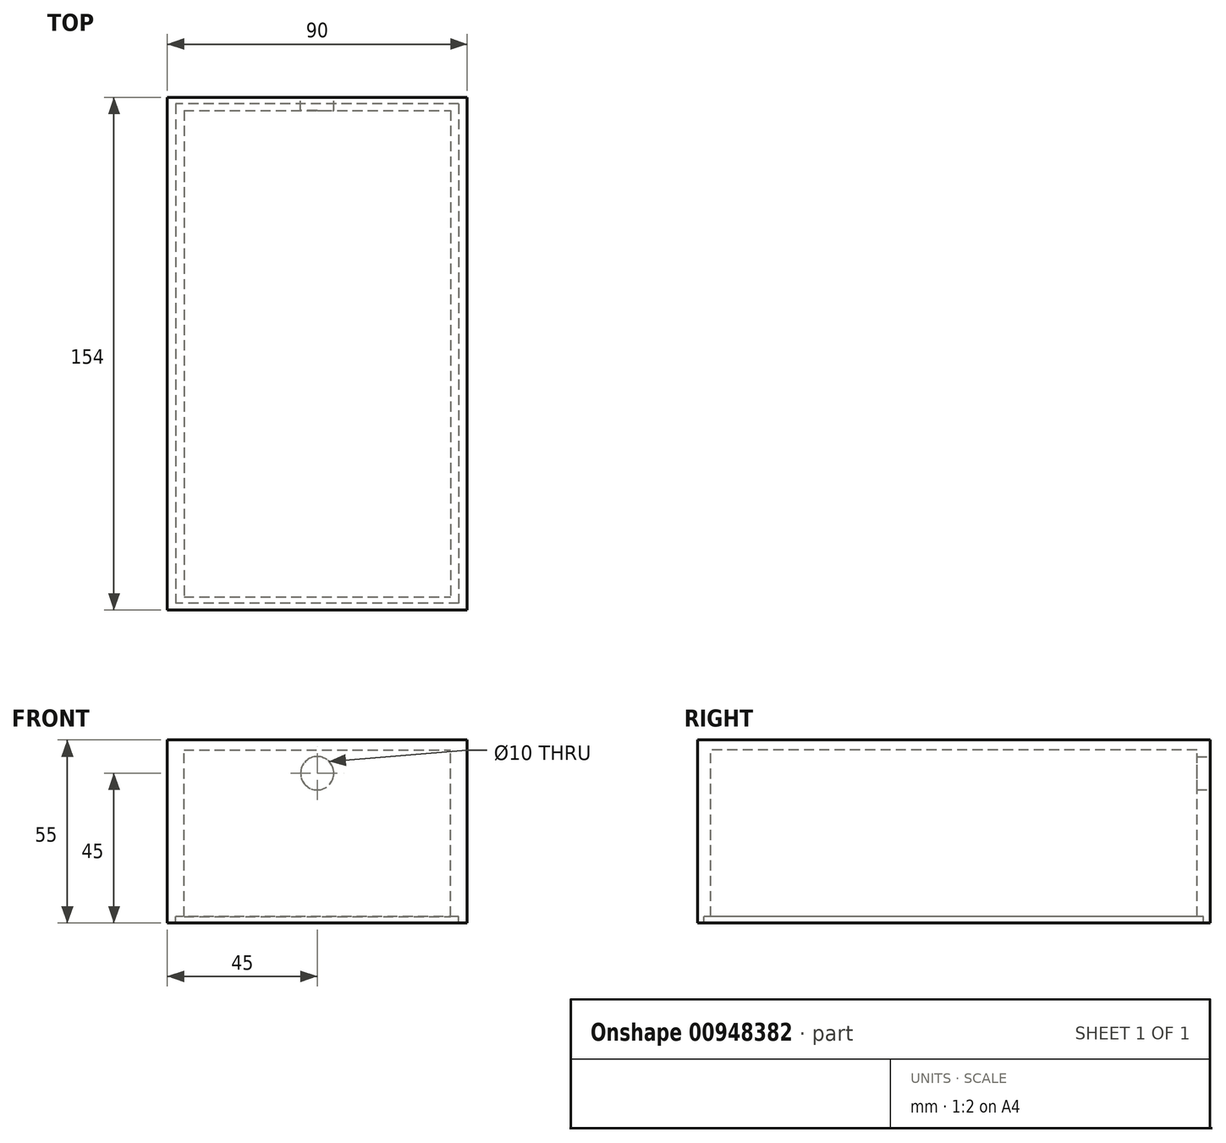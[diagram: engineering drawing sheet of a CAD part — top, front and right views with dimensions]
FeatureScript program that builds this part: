
annotation { "Feature Type Name" : "Feature", "Feature Type Description" : "" }
export const myFeature = defineFeature(function(context is Context, id is Id, definition is map)
    precondition{}
    {
        {
            var Q0;
            Q0=qCreatedBy(makeId("Top.planeOp"),FACE);
            var sketch = newSketch(context, id + "F0", { "sketchPlane" : qUnion([Q0])});
            skLineSegment(sketch, "E0.bottom", {"start": v(-45, 77) * mm, "end": v(45, 77) * mm});
            skLineSegment(sketch, "E0.top", {"start": v(-45, -77) * mm, "end": v(45, -77) * mm});
            skLineSegment(sketch, "E0.left", {"start": v(-45, 77) * mm, "end": v(-45, -77) * mm});
            skLineSegment(sketch, "E0.right", {"start": v(45, 77) * mm, "end": v(45, -77) * mm});
            skPoint(sketch, "E0.middle", {"position": v(0, 0) * mm});
            skLineSegment(sketch, "E1.bottom", {"start": v(-40, 73) * mm, "end": v(40, 73) * mm});
            skLineSegment(sketch, "E1.top", {"start": v(-40, -73) * mm, "end": v(40, -73) * mm});
            skLineSegment(sketch, "E1.left", {"start": v(-40, 73) * mm, "end": v(-40, -73) * mm});
            skLineSegment(sketch, "E1.right", {"start": v(40, 73) * mm, "end": v(40, -73) * mm});
            skLineSegment(sketch, "E2.bottom", {"start": v(42.5, 75) * mm, "end": v(-42.5, 75) * mm});
            skLineSegment(sketch, "E2.top", {"start": v(42.5, -75) * mm, "end": v(-42.5, -75) * mm});
            skLineSegment(sketch, "E2.left", {"start": v(42.5, 75) * mm, "end": v(42.5, -75) * mm});
            skLineSegment(sketch, "E2.right", {"start": v(-42.5, 75) * mm, "end": v(-42.5, -75) * mm});
            skSolve(sketch);
        }
        {
            var Q0;
            Q0=makeQuery(id+"F0.imprint","IMPRINT",FACE,{"disambiguationData":[TD([[makeQuery(id+"F0.imprint","IMPRINT",EDGE,{"derivedFrom":sQuery(id+"F0.wireOp",EDGE,"E1.bottom")}),-1.0]])]});
            var Q1;
            Q1=makeQuery(id+"F0.imprint","IMPRINT",FACE,{"disambiguationData":[TD([[makeQuery(id+"F0.imprint","IMPRINT",EDGE,{"derivedFrom":sQuery(id+"F0.wireOp",EDGE,"E1.bottom")}),1.0]])]});
            var Q2;
            Q2=makeQuery(id+"F0.imprint","IMPRINT",FACE,{"disambiguationData":[TD([[makeQuery(id+"F0.imprint","IMPRINT",EDGE,{"derivedFrom":sQuery(id+"F0.wireOp",EDGE,"E0.bottom")}),-1.0]])]});
            extrude(context, id + "F1", {"entities" : qUnion([Q0, Q1, Q2]), "depth" : 3 * mm, "offsetDistance" : 25 * mm});
        }
        {
            var Q0;
            Q0=makeQuery(id+"F0.imprint","IMPRINT",FACE,{"disambiguationData":[TD([[makeQuery(id+"F0.imprint","IMPRINT",EDGE,{"derivedFrom":sQuery(id+"F0.wireOp",EDGE,"E1.bottom")}),1.0]])]});
            var Q1;
            Q1=makeQuery(id+"F0.imprint","IMPRINT",FACE,{"disambiguationData":[TD([[makeQuery(id+"F0.imprint","IMPRINT",EDGE,{"derivedFrom":sQuery(id+"F0.wireOp",EDGE,"E0.bottom")}),-1.0]])]});
            extrude(context, id + "F2", {"entities" : qUnion([Q0, Q1]), "operationType" : NewBodyOperationType.ADD, "oppositeDirection" : true, "depth" : 50 * mm, "offsetDistance" : 25 * mm});
        }
        {
            var Q0;
            Q0=makeQuery(id+"F0.imprint","IMPRINT",FACE,{"disambiguationData":[TD([[makeQuery(id+"F0.imprint","IMPRINT",EDGE,{"derivedFrom":sQuery(id+"F0.wireOp",EDGE,"E0.bottom")}),-1.0]])]});
            extrude(context, id + "F3", {"entities" : qUnion([Q0]), "operationType" : NewBodyOperationType.ADD, "oppositeDirection" : true, "depth" : 52 * mm, "offsetDistance" : 25 * mm});
        }
        {
            var Q0;
            {var subQ0=sQuery(id+"F0.wireOp",EDGE,"E0.bottom");Q0=makeQuery(id+"F3.boolean.opBoolean","MERGE",FACE,{"derivedFrom":[makeQuery(id+"F2.boolean.opBoolean","MERGE",FACE,{"derivedFrom":[makeQuery(id+"F1.opExtrude","SWEPT_FACE",FACE,{"disambiguationData":[OSD([subQ0])]}),makeQuery(id+"F2.opExtrude","SWEPT_FACE",FACE,{"disambiguationData":[OSD([subQ0])]})]}),makeQuery(id+"F3.opExtrude","SWEPT_FACE",FACE,{"disambiguationData":[OSD([subQ0])]})]});}
            var sketch = newSketch(context, id + "F4", { "sketchPlane" : qUnion([Q0])});
            skLineSegment(sketch, "E3", {"start": v(0, 0) * mm, "end": v(0, -7) * mm, "construction": true});
            skCircle(sketch, "E4", {"center": v(0, -7) * mm, "radius": 5 * mm});
            skSolve(sketch);
        }
        {
            var Q0;
            Q0=makeQuery(id+"F4.imprint","IMPRINT",FACE,{"disambiguationData":[TD([[makeQuery(id+"F4.imprint","IMPRINT",EDGE,{"derivedFrom":sQuery(id+"F4.wireOp",EDGE,"E4")}),1.0]])]});
            extrude(context, id + "F5", {"entities" : qUnion([Q0]), "operationType" : NewBodyOperationType.REMOVE, "oppositeDirection" : true, "depth" : 5 * mm, "offsetDistance" : 25 * mm});
        }
    });
